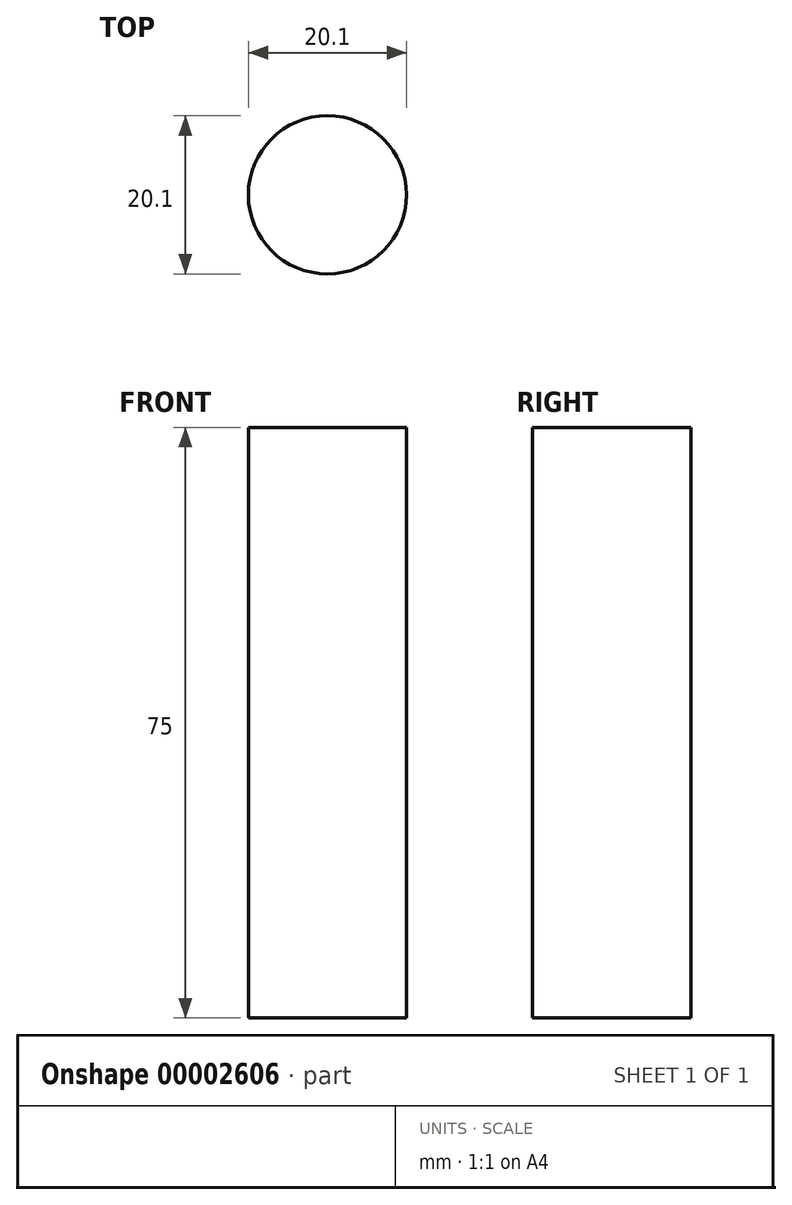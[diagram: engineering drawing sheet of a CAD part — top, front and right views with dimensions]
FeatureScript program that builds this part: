
annotation { "Feature Type Name" : "Feature", "Feature Type Description" : "" }
export const myFeature = defineFeature(function(context is Context, id is Id, definition is map)
    precondition{}
    {
        {
            var Q0;
            Q0=qCreatedBy(makeId("Top.planeOp"),FACE);
            var sketch = newSketch(context, id + "F0", { "sketchPlane" : qUnion([Q0])});
            skCircle(sketch, "E0", {"center": v(0, 0) * mm, "radius": 10.05 * mm});
            skSolve(sketch);
        }
        {
            var Q0;
            Q0 = qSketchRegion(id + "F0", true);
            extrude(context, id + "F1", {"entities" : qUnion([Q0]), "depth" : 75 * mm});
        }
    });
